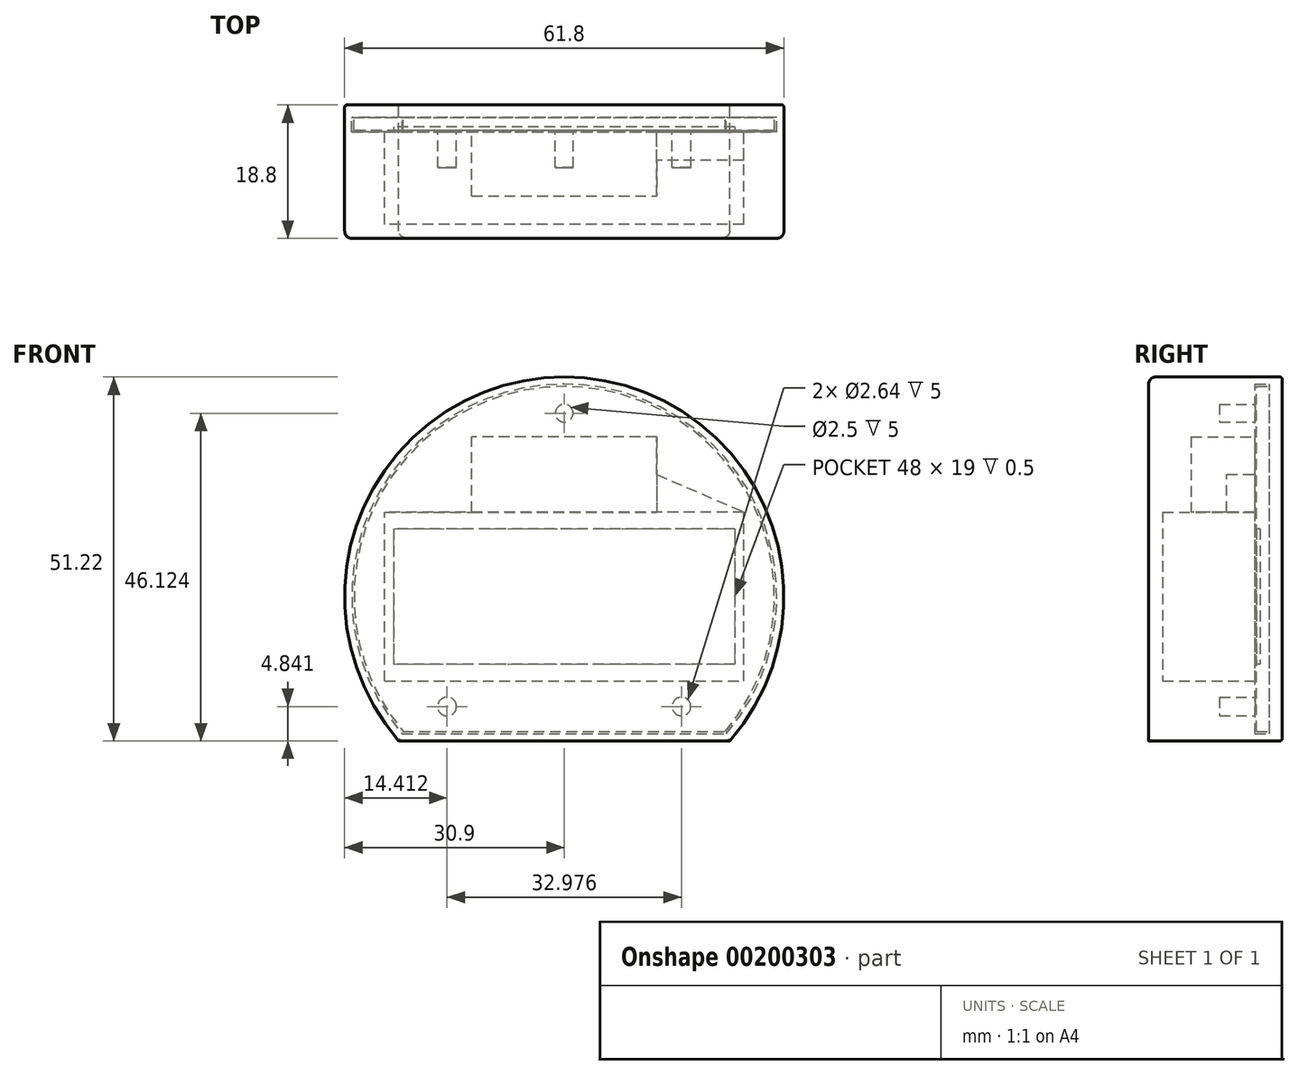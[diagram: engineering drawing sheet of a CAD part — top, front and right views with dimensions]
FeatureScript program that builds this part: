
annotation { "Feature Type Name" : "Feature", "Feature Type Description" : "" }
export const myFeature = defineFeature(function(context is Context, id is Id, definition is map)
    precondition{}
    {
        {
            var Q0;
            Q0=qCreatedBy(makeId("Front.planeOp"),FACE);
            var sketch = newSketch(context, id + "F0", { "sketchPlane" : qUnion([Q0])});
            skCircle(sketch, "E0", {"center": v(0, 0) * mm, "radius": 30.9 * mm});
            skSolve(sketch);
        }
        {
            var Q0;
            Q0 = qSketchRegion(id + "F0", true);
            extrude(context, id + "F1", {"entities" : qUnion([Q0]), "depth" : 17 * mm});
        }
        {
            var Q0;
            Q0=qCreatedBy(makeId("Front.planeOp"),FACE);
            var sketch = newSketch(context, id + "F2", { "sketchPlane" : qUnion([Q0])});
            skLineSegment(sketch, "E1.bottom", {"start": v(25.25, 11.9) * mm, "end": v(-25.25, 11.9) * mm});
            skLineSegment(sketch, "E1.top", {"start": v(25.25, -11.9) * mm, "end": v(-25.25, -11.9) * mm});
            skLineSegment(sketch, "E1.left", {"start": v(25.25, 11.9) * mm, "end": v(25.25, -11.9) * mm});
            skLineSegment(sketch, "E1.right", {"start": v(-25.25, 11.9) * mm, "end": v(-25.25, -11.9) * mm});
            skPoint(sketch, "E1.middle", {"position": v(0, 0) * mm});
            skSolve(sketch);
        }
        {
            var Q0;
            Q0 = qSketchRegion(id + "F2", true);
            extrude(context, id + "F3", {"entities" : qUnion([Q0]), "operationType" : NewBodyOperationType.REMOVE, "depth" : 15 * mm});
        }
        {
            var Q0;
            Q0=makeQuery(id+"F1.opExtrude","CAP_FACE",FACE,{"disambiguationData":[OSD([sQuery(id+"F0.wireOp",EDGE,"E0")])],"isStart":true});
            var sketch = newSketch(context, id + "F4", { "sketchPlane" : qUnion([Q0])});
            skLineSegment(sketch, "E2.bottom", {"start": v(13, 22.45) * mm, "end": v(-13, 22.45) * mm});
            skLineSegment(sketch, "E2.top", {"start": v(13, 10.95) * mm, "end": v(-13, 10.95) * mm});
            skLineSegment(sketch, "E2.left", {"start": v(13, 22.45) * mm, "end": v(13, 10.95) * mm});
            skLineSegment(sketch, "E2.right", {"start": v(-13, 22.45) * mm, "end": v(-13, 10.95) * mm});
            skPoint(sketch, "E2.middle", {"position": v(0, 16.7) * mm});
            skPoint(sketch, "E2.middle.positionSnap0", {"position": v(0, 11.9) * mm});
            skPoint(sketch, "E2.centerSnap0", {"position": v(0, 11.9) * mm});
            skSolve(sketch);
        }
        {
            var Q0;
            Q0 = qSketchRegion(id + "F4", true);
            extrude(context, id + "F5", {"entities" : qUnion([Q0]), "operationType" : NewBodyOperationType.REMOVE, "oppositeDirection" : true, "depth" : 11 * mm});
        }
        {
            var Q0;
            Q0=makeQuery(id+"F1.opExtrude","CAP_FACE",FACE,{"disambiguationData":[OSD([sQuery(id+"F0.wireOp",EDGE,"E0")])],"isStart":true});
            var sketch = newSketch(context, id + "F6", { "sketchPlane" : qUnion([Q0])});
            skLineSegment(sketch, "E3", {"start": v(-25.25, 11.9) * mm, "end": v(-13, 17.17) * mm});
            skLineSegment(sketch, "E4", {"start": v(-13, 17.17) * mm, "end": v(-13, 11.9) * mm});
            skLineSegment(sketch, "E5", {"start": v(-13, 11.9) * mm, "end": v(-25.25, 11.9) * mm});
            skSolve(sketch);
        }
        {
            var Q0;
            Q0 = qSketchRegion(id + "F6", true);
            extrude(context, id + "F7", {"entities" : qUnion([Q0]), "operationType" : NewBodyOperationType.REMOVE, "oppositeDirection" : true, "depth" : 6 * mm});
        }
        {
            var Q0;
            Q0=makeQuery(id+"F1.opExtrude","CAP_FACE",FACE,{"disambiguationData":[OSD([sQuery(id+"F0.wireOp",EDGE,"E0")])],"isStart":true});
            var sketch = newSketch(context, id + "F8", { "sketchPlane" : qUnion([Q0])});
            skLineSegment(sketch, "E6.bottom", {"start": v(31.4, -20.32) * mm, "end": v(-31.4, -20.32) * mm});
            skLineSegment(sketch, "E6.top", {"start": v(31.4, -41.48) * mm, "end": v(-31.4, -41.48) * mm});
            skLineSegment(sketch, "E6.left", {"start": v(31.4, -20.32) * mm, "end": v(31.4, -41.48) * mm});
            skLineSegment(sketch, "E6.right", {"start": v(-31.4, -20.32) * mm, "end": v(-31.4, -41.48) * mm});
            skPoint(sketch, "E6.middle", {"position": v(0, -30.9) * mm});
            skSolve(sketch);
        }
        {
            var Q0;
            Q0 = qSketchRegion(id + "F8", true);
            extrude(context, id + "F9", {"entities" : qUnion([Q0]), "operationType" : NewBodyOperationType.REMOVE, "endBound" : BoundingType.THROUGH_ALL, "oppositeDirection" : true, "depth" : 25 * mm});
        }
        {
            var Q0;
            Q0=makeQuery(id+"F1.opExtrude","CAP_FACE",FACE,{"disambiguationData":[OSD([sQuery(id+"F0.wireOp",EDGE,"E0")])],"isStart":true});
            var sketch = newSketch(context, id + "F10", { "sketchPlane" : qUnion([Q0])});
            skArc(sketch, "E7.0", {"start": v(-23.28, -20.32) * mm, "mid": v(0, 30.9) * mm, "end": v(23.28, -20.32) * mm, "construction": true});
            skLineSegment(sketch, "E7.1", {"start": v(23.28, -20.32) * mm, "end": v(-23.28, -20.32) * mm, "construction": true});
            skLineSegment(sketch, "E8.0", {"start": v(22.82, -19.32) * mm, "end": v(-22.82, -19.32) * mm});
            skArc(sketch, "E8.1", {"start": v(-22.82, -19.32) * mm, "mid": v(0, 29.9) * mm, "end": v(22.82, -19.32) * mm});
            skSolve(sketch);
        }
        {
            var Q0;
            Q0 = qSketchRegion(id + "F10", true);
            extrude(context, id + "F11", {"entities" : qUnion([Q0]), "operationType" : NewBodyOperationType.REMOVE, "oppositeDirection" : true, "depth" : 2 * mm});
        }
        {
            var Q0;
            Q0=qCreatedBy(makeId("Front.planeOp"),FACE);
            var sketch = newSketch(context, id + "F12", { "sketchPlane" : qUnion([Q0])});
            skArc(sketch, "E9.0", {"start": v(22.69, -18.97) * mm, "mid": v(0, 29.57) * mm, "end": v(-22.69, -18.97) * mm});
            skLineSegment(sketch, "E9.1", {"start": v(-22.69, -18.97) * mm, "end": v(22.69, -18.97) * mm});
            skSolve(sketch);
        }
        {
            var Q0;
            Q0 = qSketchRegion(id + "F12", true);
            extrude(context, id + "F13", {"entities" : qUnion([Q0]), "depth" : 1.8 * mm, "hasSecondDirection" : true, "secondDirectionOppositeDirection" : true, "secondDirectionDepth" : 1.8 * mm});
        }
        {
            var Q0;
            Q0=makeQuery(id+"F13.opExtrude","CAP_FACE",FACE,{"disambiguationData":[OSD([sQuery(id+"F12.wireOp",EDGE,"E9.0"),sQuery(id+"F12.wireOp",EDGE,"E9.1")])],"isStart":true});
            var sketch = newSketch(context, id + "F14", { "sketchPlane" : qUnion([Q0])});
            skArc(sketch, "E10.0", {"start": v(-23.28, -20.32) * mm, "mid": v(0, 30.9) * mm, "end": v(23.28, -20.32) * mm});
            skLineSegment(sketch, "E11.0", {"start": v(23.28, -20.32) * mm, "end": v(-23.28, -20.32) * mm});
            skSolve(sketch);
        }
        {
            var Q0;
            Q0 = qSketchRegion(id + "F14", true);
            extrude(context, id + "F15", {"entities" : qUnion([Q0]), "operationType" : NewBodyOperationType.ADD, "oppositeDirection" : true, "depth" : 1.8 * mm});
        }
        {
            var Q0;
            Q0=makeQuery(id+"F1.opExtrude","CAP_EDGE",EDGE,{"disambiguationData":[OSD([sQuery(id+"F0.wireOp",EDGE,"E0")])],"isStart":false});
            fillet(context, id + "F16", {"entities" : qUnion([Q0]), "radius" : 1 * mm, "tangentPropagation" : true, "allowEdgeOverflow" : false});
        }
        {
            var Q0;
            Q0=makeQuery(id+"F11.boolean.opBoolean","COPY",FACE,{"derivedFrom":makeQuery(id+"F11.opExtrude","CAP_FACE",FACE,{"disambiguationData":[OSD([sQuery(id+"F10.wireOp",EDGE,"E8.0"),sQuery(id+"F10.wireOp",EDGE,"E8.1")])],"isStart":false})});
            var sketch = newSketch(context, id + "F17", { "sketchPlane" : qUnion([Q0])});
            skCircle(sketch, "E12", {"center": v(-16.49, -15.48) * mm, "radius": 1.32 * mm});
            skCircle(sketch, "E13", {"center": v(0, 25.8) * mm, "radius": 1.25 * mm});
            skLineSegment(sketch, "E14", {"start": v(0, 0) * mm, "end": v(0, -11.9) * mm, "construction": true});
            skCircle(sketch, "E15.MirrorC", {"center": v(16.49, -15.48) * mm, "radius": 1.32 * mm});
            skSolve(sketch);
        }
        {
            var Q0;
            Q0 = qSketchRegion(id + "F17", true);
            extrude(context, id + "F18", {"entities" : qUnion([Q0]), "operationType" : NewBodyOperationType.REMOVE, "oppositeDirection" : true, "depth" : 5 * mm});
        }
        {
            var Q0;
            Q0=makeQuery(id+"F13.opExtrude","CAP_FACE",FACE,{"disambiguationData":[OSD([sQuery(id+"F12.wireOp",EDGE,"E9.0"),sQuery(id+"F12.wireOp",EDGE,"E9.1")])],"isStart":false});
            var sketch = newSketch(context, id + "F19", { "sketchPlane" : qUnion([Q0])});
            skLineSegment(sketch, "E16.bottom", {"start": v(24, 9.5) * mm, "end": v(-24, 9.5) * mm});
            skLineSegment(sketch, "E16.top", {"start": v(24, -9.5) * mm, "end": v(-24, -9.5) * mm});
            skLineSegment(sketch, "E16.left", {"start": v(24, 9.5) * mm, "end": v(24, -9.5) * mm});
            skLineSegment(sketch, "E16.right", {"start": v(-24, 9.5) * mm, "end": v(-24, -9.5) * mm});
            skPoint(sketch, "E16.middle", {"position": v(0, 0) * mm});
            skSolve(sketch);
        }
        {
            var Q0;
            Q0 = qSketchRegion(id + "F19", true);
            extrude(context, id + "F20", {"entities" : qUnion([Q0]), "operationType" : NewBodyOperationType.REMOVE, "oppositeDirection" : true, "depth" : 0.5 * mm});
        }
        {
            var Q0;
            Q0=makeQuery(id+"F15.boolean.opBoolean","MERGE",FACE,{"derivedFrom":[makeQuery(id+"F13.opExtrude","CAP_FACE",FACE,{"disambiguationData":[OSD([sQuery(id+"F12.wireOp",EDGE,"E9.0"),sQuery(id+"F12.wireOp",EDGE,"E9.1")])],"isStart":true}),makeQuery(id+"F15.opExtrude","CAP_FACE",FACE,{"disambiguationData":[OSD([sQuery(id+"F14.wireOp",EDGE,"E10.0"),sQuery(id+"F14.wireOp",EDGE,"E11.0")])],"isStart":true})]});
            fillet(context, id + "F21", {"entities" : qUnion([Q0]), "radius" : 0.3 * mm, "tangentPropagation" : true, "allowEdgeOverflow" : false});
        }
    });
